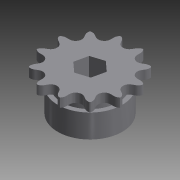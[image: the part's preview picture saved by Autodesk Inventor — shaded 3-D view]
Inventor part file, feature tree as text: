
AUTODESK INVENTOR PART (.ipt)
format: ipt  version: 2013 (Build 170138000, 138)  size: 231,936 bytes
history: native  units: mm (DEFAULTED — no unit token found)
features: imported_body x1, extrude x1, sketch x1
ambient origin geometry x8: Origin, YZ Plane, XZ Plane, XY Plane, X Axis, Y Axis, Z Axis, Center Point
bodies: Solid1 (feature_tree)
feature tree (3):
  imported_body  "Base1"
  extrude  "Extrusion1"  [1 undecoded]
  sketch  "Sketch1"  dims[d0=19.2532mm d1=0.0mm]
note: 1 required parameter value undecoded (feature->parameter linkage not recoverable at this tier; creation-order binding heuristic only, values carry confidence <= 0.55)
